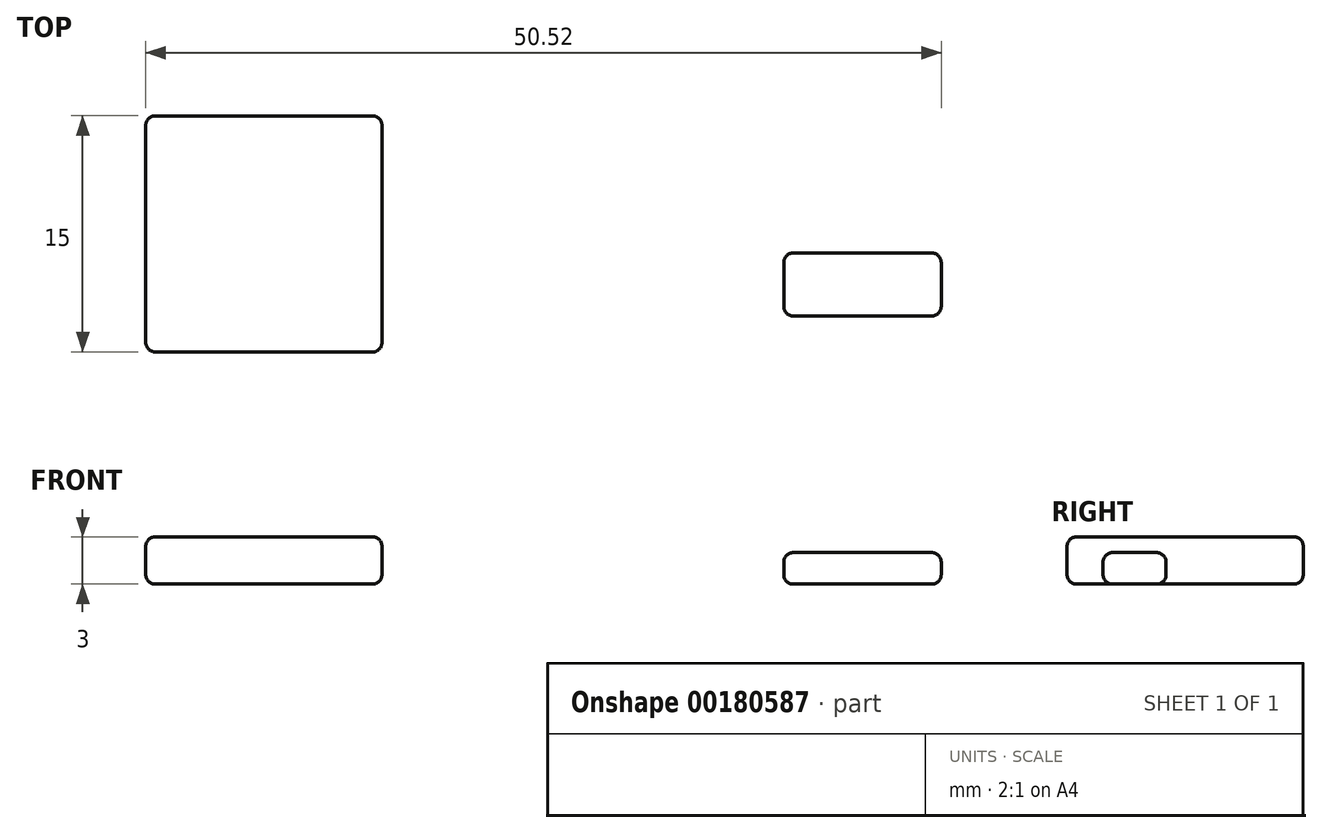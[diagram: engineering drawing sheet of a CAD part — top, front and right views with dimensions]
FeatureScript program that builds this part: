
annotation { "Feature Type Name" : "Feature", "Feature Type Description" : "" }
export const myFeature = defineFeature(function(context is Context, id is Id, definition is map)
    precondition{}
    {
        {
            var Q0;
            Q0=qCreatedBy(makeId("Top.planeOp"),FACE);
            var sketch = newSketch(context, id + "F0", { "sketchPlane" : qUnion([Q0])});
            skLineSegment(sketch, "E0.bottom", {"start": v(-50.52, 23) * mm, "end": v(-35.52, 23) * mm});
            skLineSegment(sketch, "E0.top", {"start": v(-50.52, 8) * mm, "end": v(-35.52, 8) * mm});
            skLineSegment(sketch, "E0.left", {"start": v(-50.52, 23) * mm, "end": v(-50.52, 8) * mm});
            skLineSegment(sketch, "E0.right", {"start": v(-35.52, 23) * mm, "end": v(-35.52, 8) * mm});
            skLineSegment(sketch, "E1.bottom", {"start": v(-10, 14.28) * mm, "end": v(0, 14.28) * mm});
            skLineSegment(sketch, "E1.top", {"start": v(-10, 10.28) * mm, "end": v(0, 10.28) * mm});
            skLineSegment(sketch, "E1.left", {"start": v(-10, 14.28) * mm, "end": v(-10, 10.28) * mm});
            skLineSegment(sketch, "E1.right", {"start": v(0, 14.28) * mm, "end": v(0, 10.28) * mm});
            skSolve(sketch);
        }
        {
            var Q0;
            Q0=makeQuery(id+"F0.imprint","IMPRINT",FACE,{"disambiguationData":[TD([[makeQuery(id+"F0.imprint","IMPRINT",EDGE,{"derivedFrom":sQuery(id+"F0.wireOp",EDGE,"E0.bottom")}),-1.0]])]});
            extrude(context, id + "F1", {"entities" : qUnion([Q0]), "depth" : 3 * mm});
        }
        {
            var Q0;
            Q0=makeQuery(id+"F0.imprint","IMPRINT",FACE,{"disambiguationData":[TD([[makeQuery(id+"F0.imprint","IMPRINT",EDGE,{"derivedFrom":sQuery(id+"F0.wireOp",EDGE,"E1.bottom")}),-1.0]])]});
            extrude(context, id + "F2", {"entities" : qUnion([Q0]), "depth" : 2 * mm});
        }
        {
            var Q0;
            Q0=makeQuery(id+"F1.opExtrude","SWEPT_FACE",FACE,{"disambiguationData":[OSD([sQuery(id+"F0.wireOp",EDGE,"E0.left")])]});
            var Q1;
            Q1=makeQuery(id+"F1.opExtrude","CAP_EDGE",EDGE,{"disambiguationData":[OSD([sQuery(id+"F0.wireOp",EDGE,"E0.bottom")])],"isStart":false});
            var Q2;
            Q2=makeQuery(id+"F1.opExtrude","SWEPT_FACE",FACE,{"disambiguationData":[OSD([sQuery(id+"F0.wireOp",EDGE,"E0.right")])]});
            var Q3;
            Q3=makeQuery(id+"F1.opExtrude","CAP_FACE",FACE,{"disambiguationData":[OSD([sQuery(id+"F0.wireOp",EDGE,"E0.bottom"),sQuery(id+"F0.wireOp",EDGE,"E0.top"),sQuery(id+"F0.wireOp",EDGE,"E0.left"),sQuery(id+"F0.wireOp",EDGE,"E0.right")])],"isStart":false});
            var Q4;
            Q4=makeQuery(id+"F1.opExtrude","SWEPT_EDGE",EDGE,{"disambiguationData":[OSD([sQuery(id+"F0.wireOp",EDGE,"E0.top"),sQuery(id+"F0.wireOp",EDGE,"E0.left")])]});
            var Q5;
            Q5=makeQuery(id+"F1.opExtrude","SWEPT_EDGE",EDGE,{"disambiguationData":[OSD([sQuery(id+"F0.wireOp",EDGE,"E0.bottom"),sQuery(id+"F0.wireOp",EDGE,"E0.right")])]});
            var Q6;
            Q6=makeQuery(id+"F1.opExtrude","SWEPT_FACE",FACE,{"disambiguationData":[OSD([sQuery(id+"F0.wireOp",EDGE,"E0.bottom")])]});
            var Q7;
            Q7=makeQuery(id+"F1.opExtrude","SWEPT_EDGE",EDGE,{"disambiguationData":[OSD([sQuery(id+"F0.wireOp",EDGE,"E0.bottom"),sQuery(id+"F0.wireOp",EDGE,"E0.left")])]});
            var Q8;
            Q8=makeQuery(id+"F2.opExtrude","CAP_EDGE",EDGE,{"disambiguationData":[OSD([sQuery(id+"F0.wireOp",EDGE,"E1.top")])],"isStart":false});
            var Q9;
            Q9=makeQuery(id+"F2.opExtrude","SWEPT_FACE",FACE,{"disambiguationData":[OSD([sQuery(id+"F0.wireOp",EDGE,"E1.right")])]});
            var Q10;
            Q10=makeQuery(id+"F2.opExtrude","SWEPT_FACE",FACE,{"disambiguationData":[OSD([sQuery(id+"F0.wireOp",EDGE,"E1.left")])]});
            var Q11;
            Q11=makeQuery(id+"F2.opExtrude","CAP_FACE",FACE,{"disambiguationData":[OSD([sQuery(id+"F0.wireOp",EDGE,"E1.bottom"),sQuery(id+"F0.wireOp",EDGE,"E1.top"),sQuery(id+"F0.wireOp",EDGE,"E1.left"),sQuery(id+"F0.wireOp",EDGE,"E1.right")])],"isStart":false});
            var Q12;
            Q12=makeQuery(id+"F2.opExtrude","SWEPT_EDGE",EDGE,{"disambiguationData":[OSD([sQuery(id+"F0.wireOp",EDGE,"E1.top"),sQuery(id+"F0.wireOp",EDGE,"E1.left")])]});
            var Q13;
            Q13=makeQuery(id+"F2.opExtrude","SWEPT_EDGE",EDGE,{"disambiguationData":[OSD([sQuery(id+"F0.wireOp",EDGE,"E1.bottom"),sQuery(id+"F0.wireOp",EDGE,"E1.right")])]});
            var Q14;
            Q14=makeQuery(id+"F2.opExtrude","SWEPT_FACE",FACE,{"disambiguationData":[OSD([sQuery(id+"F0.wireOp",EDGE,"E1.bottom")])]});
            var Q15;
            Q15=makeQuery(id+"F2.opExtrude","SWEPT_EDGE",EDGE,{"disambiguationData":[OSD([sQuery(id+"F0.wireOp",EDGE,"E1.bottom"),sQuery(id+"F0.wireOp",EDGE,"E1.left")])]});
            var Q16;
            Q16=makeQuery(id+"F1.opExtrude","CAP_EDGE",EDGE,{"disambiguationData":[OSD([sQuery(id+"F0.wireOp",EDGE,"E0.bottom")])],"isStart":true});
            var Q17;
            Q17=makeQuery(id+"F1.opExtrude","CAP_EDGE",EDGE,{"disambiguationData":[OSD([sQuery(id+"F0.wireOp",EDGE,"E0.top")])],"isStart":true});
            var Q18;
            Q18=makeQuery(id+"F1.opExtrude","CAP_EDGE",EDGE,{"disambiguationData":[OSD([sQuery(id+"F0.wireOp",EDGE,"E0.top")])],"isStart":false});
            var Q19;
            Q19=makeQuery(id+"F1.opExtrude","CAP_EDGE",EDGE,{"disambiguationData":[OSD([sQuery(id+"F0.wireOp",EDGE,"E0.left")])],"isStart":true});
            var Q20;
            Q20=makeQuery(id+"F1.opExtrude","CAP_EDGE",EDGE,{"disambiguationData":[OSD([sQuery(id+"F0.wireOp",EDGE,"E0.left")])],"isStart":false});
            var Q21;
            Q21=makeQuery(id+"F1.opExtrude","CAP_EDGE",EDGE,{"disambiguationData":[OSD([sQuery(id+"F0.wireOp",EDGE,"E0.right")])],"isStart":true});
            var Q22;
            Q22=makeQuery(id+"F1.opExtrude","SWEPT_FACE",FACE,{"disambiguationData":[OSD([sQuery(id+"F0.wireOp",EDGE,"E0.top")])]});
            var Q23;
            Q23=makeQuery(id+"F1.opExtrude","SWEPT_EDGE",EDGE,{"disambiguationData":[OSD([sQuery(id+"F0.wireOp",EDGE,"E0.top"),sQuery(id+"F0.wireOp",EDGE,"E0.right")])]});
            var Q24;
            Q24=makeQuery(id+"F1.opExtrude","CAP_FACE",FACE,{"disambiguationData":[OSD([sQuery(id+"F0.wireOp",EDGE,"E0.bottom"),sQuery(id+"F0.wireOp",EDGE,"E0.top"),sQuery(id+"F0.wireOp",EDGE,"E0.left"),sQuery(id+"F0.wireOp",EDGE,"E0.right")])],"isStart":true});
            var Q25;
            Q25=makeQuery(id+"F1.opExtrude","CAP_EDGE",EDGE,{"disambiguationData":[OSD([sQuery(id+"F0.wireOp",EDGE,"E0.right")])],"isStart":false});
            var Q26;
            Q26=makeQuery(id+"F2.opExtrude","CAP_EDGE",EDGE,{"disambiguationData":[OSD([sQuery(id+"F0.wireOp",EDGE,"E1.right")])],"isStart":false});
            var Q27;
            Q27=makeQuery(id+"F2.opExtrude","CAP_EDGE",EDGE,{"disambiguationData":[OSD([sQuery(id+"F0.wireOp",EDGE,"E1.right")])],"isStart":true});
            var Q28;
            Q28=makeQuery(id+"F2.opExtrude","CAP_EDGE",EDGE,{"disambiguationData":[OSD([sQuery(id+"F0.wireOp",EDGE,"E1.left")])],"isStart":false});
            var Q29;
            Q29=makeQuery(id+"F2.opExtrude","CAP_EDGE",EDGE,{"disambiguationData":[OSD([sQuery(id+"F0.wireOp",EDGE,"E1.left")])],"isStart":true});
            var Q30;
            Q30=makeQuery(id+"F2.opExtrude","CAP_EDGE",EDGE,{"disambiguationData":[OSD([sQuery(id+"F0.wireOp",EDGE,"E1.top")])],"isStart":true});
            var Q31;
            Q31=makeQuery(id+"F2.opExtrude","CAP_EDGE",EDGE,{"disambiguationData":[OSD([sQuery(id+"F0.wireOp",EDGE,"E1.bottom")])],"isStart":false});
            var Q32;
            Q32=makeQuery(id+"F2.opExtrude","CAP_EDGE",EDGE,{"disambiguationData":[OSD([sQuery(id+"F0.wireOp",EDGE,"E1.bottom")])],"isStart":true});
            var Q33;
            Q33=makeQuery(id+"F2.opExtrude","SWEPT_FACE",FACE,{"disambiguationData":[OSD([sQuery(id+"F0.wireOp",EDGE,"E1.top")])]});
            var Q34;
            Q34=makeQuery(id+"F2.opExtrude","SWEPT_EDGE",EDGE,{"disambiguationData":[OSD([sQuery(id+"F0.wireOp",EDGE,"E1.top"),sQuery(id+"F0.wireOp",EDGE,"E1.right")])]});
            var Q35;
            Q35=makeQuery(id+"F2.opExtrude","CAP_FACE",FACE,{"disambiguationData":[OSD([sQuery(id+"F0.wireOp",EDGE,"E1.bottom"),sQuery(id+"F0.wireOp",EDGE,"E1.top"),sQuery(id+"F0.wireOp",EDGE,"E1.left"),sQuery(id+"F0.wireOp",EDGE,"E1.right")])],"isStart":true});
            fillet(context, id + "F3", {"entities" : qUnion([Q0, Q1, Q2, Q3, Q4, Q5, Q6, Q7, Q8, Q9, Q10, Q11, Q12, Q13, Q14, Q15, Q16, Q17, Q18, Q19, Q20, Q21, Q22, Q23, Q24, Q25, Q26, Q27, Q28, Q29, Q30, Q31, Q32, Q33, Q34, Q35]), "radius" : 0.6 * mm, "tangentPropagation" : true, "allowEdgeOverflow" : false});
        }
    });
